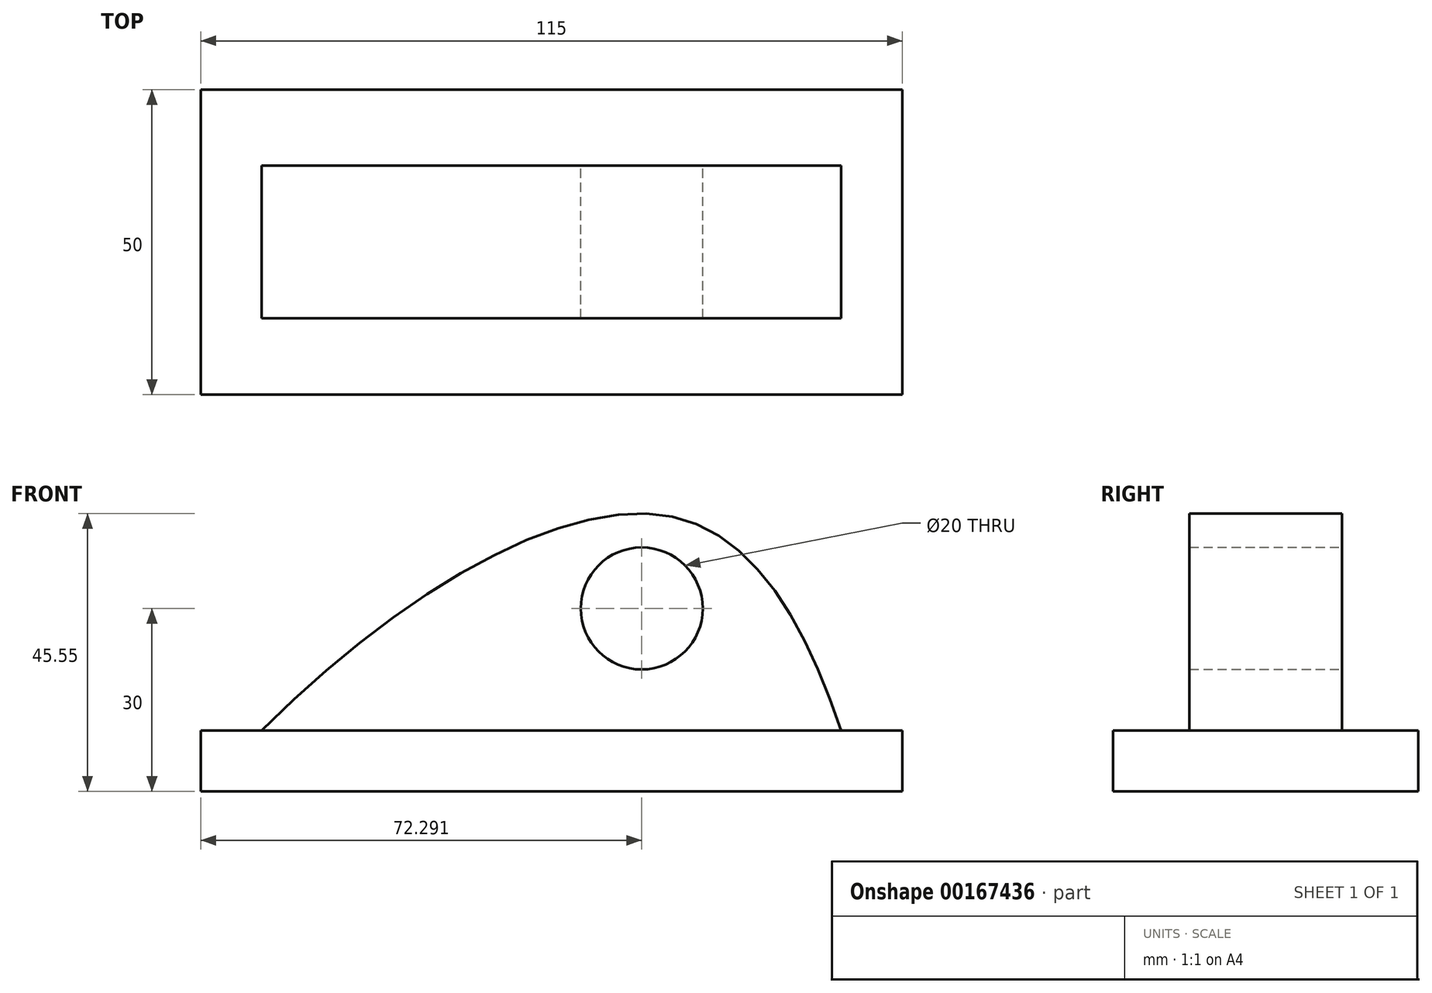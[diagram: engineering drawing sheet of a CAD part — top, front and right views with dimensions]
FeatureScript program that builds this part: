
annotation { "Feature Type Name" : "Feature", "Feature Type Description" : "" }
export const myFeature = defineFeature(function(context is Context, id is Id, definition is map)
    precondition{}
    {
        {
            var Q0;
            Q0=qCreatedBy(makeId("Front.planeOp"),FACE);
            var sketch = newSketch(context, id + "F0", { "sketchPlane" : qUnion([Q0])});
            skFitSpline(sketch, "E0", {"points": [v(-33.21, 0) * mm, v(34.2, 35) * mm, v(61.79, 0) * mm], "startDerivative": vector(118.36, 118.7) * mm, "endDerivative": vector(40.52, -119.49) * mm});
            skLineSegment(sketch, "E1", {"start": v(-33.21, 0) * mm, "end": v(61.79, 0) * mm});
            skCircle(sketch, "E2", {"center": v(29.08, 20) * mm, "radius": 10 * mm});
            skLineSegment(sketch, "E3.bottom", {"start": v(-43.21, 0) * mm, "end": v(71.79, 0) * mm});
            skLineSegment(sketch, "E3.top", {"start": v(-43.21, -10) * mm, "end": v(71.79, -10) * mm});
            skLineSegment(sketch, "E3.left", {"start": v(-43.21, 0) * mm, "end": v(-43.21, -10) * mm});
            skLineSegment(sketch, "E3.right", {"start": v(71.79, 0) * mm, "end": v(71.79, -10) * mm});
            skSolve(sketch);
        }
        {
            var Q0;
            Q0=makeQuery(id+"F0.imprint","IMPRINT",FACE,{"disambiguationData":[TD([[makeQuery(id+"F0.imprint","IMPRINT",EDGE,{"derivedFrom":sQuery(id+"F0.wireOp",EDGE,"E3.top")}),1.0]])]});
            extrude(context, id + "F1", {"entities" : qUnion([Q0]), "endBound" : BoundingType.SYMMETRIC, "depth" : 50 * mm});
        }
        {
            var Q0;
            Q0 = qSketchRegion(id + "F0", true);
            extrude(context, id + "F2", {"entities" : qUnion([Q0]), "operationType" : NewBodyOperationType.ADD, "endBound" : BoundingType.SYMMETRIC, "depth" : 25 * mm});
        }
    });
